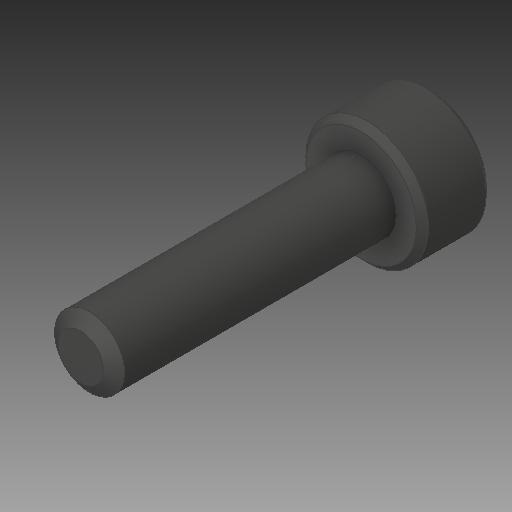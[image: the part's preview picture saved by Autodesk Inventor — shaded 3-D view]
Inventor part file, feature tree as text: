
AUTODESK INVENTOR PART (.ipt)
format: ipt  version: 2019 (Build 230136000, 136)  size: 119,296 bytes
history: native  units: in
note: dims shown in document units (in); Inventor stores cm internally (conversion verified against a paired STEP export)
features: chamfer x1
ambient origin geometry x8: Origin, YZ Plane, XZ Plane, XY Plane, X Axis, Y Axis, Z Axis, Center Point
bodies: Solid1 (feature_tree)
feature tree (1):
  chamfer  "Chamfer1"  [1 undecoded]
note: 1 required parameter value undecoded (feature->parameter linkage not recoverable at this tier; creation-order binding heuristic only, values carry confidence <= 0.55)
